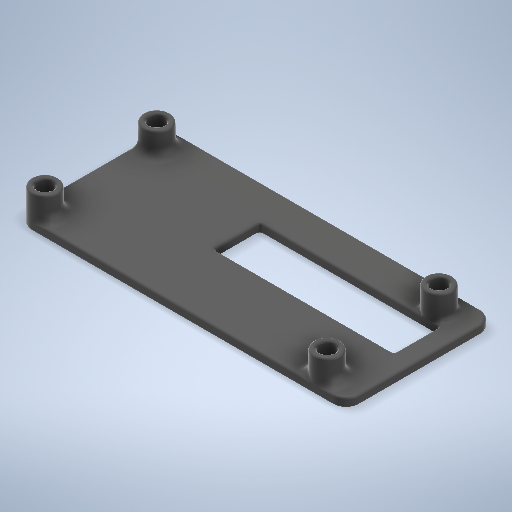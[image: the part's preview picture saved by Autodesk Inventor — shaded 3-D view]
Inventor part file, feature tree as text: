
AUTODESK INVENTOR PART (.ipt)
format: ipt  version: 2025 (Build 290162000, 162)  size: 570,368 bytes
history: native  units: mm
features: fillet x3, extrude x2, sketch x1
ambient origin geometry x8: Origin, YZ Plane, XZ Plane, XY Plane, X Axis, Y Axis, Z Axis, Center Point
bodies: Solid1 (feature_tree)
feature tree (6):
  sketch  "Sketch1"  dims[d0=3.2mm d1=58.0mm d2=23.0mm d3=5.5mm d7=2.0mm d8=0.0mm d9=5.0mm d10=0.0mm d11=0.5mm d12=37.0mm d13=9.4mm d15=2.75mm d16=4.65mm d17=6.65mm d18=11.95mm d19=0.0mm d20=2.0mm d21=1.0mm]
  extrude  "Extrusion1"  Depth=58.0mm
  extrude  "Extrusion2"  Depth=23.0mm
  fillet  "Fillet1"  Radius=5.5mm
  fillet  "Fillet2"  Radius=2.0mm
  fillet  "Fillet3"  Radius=5.0mm
